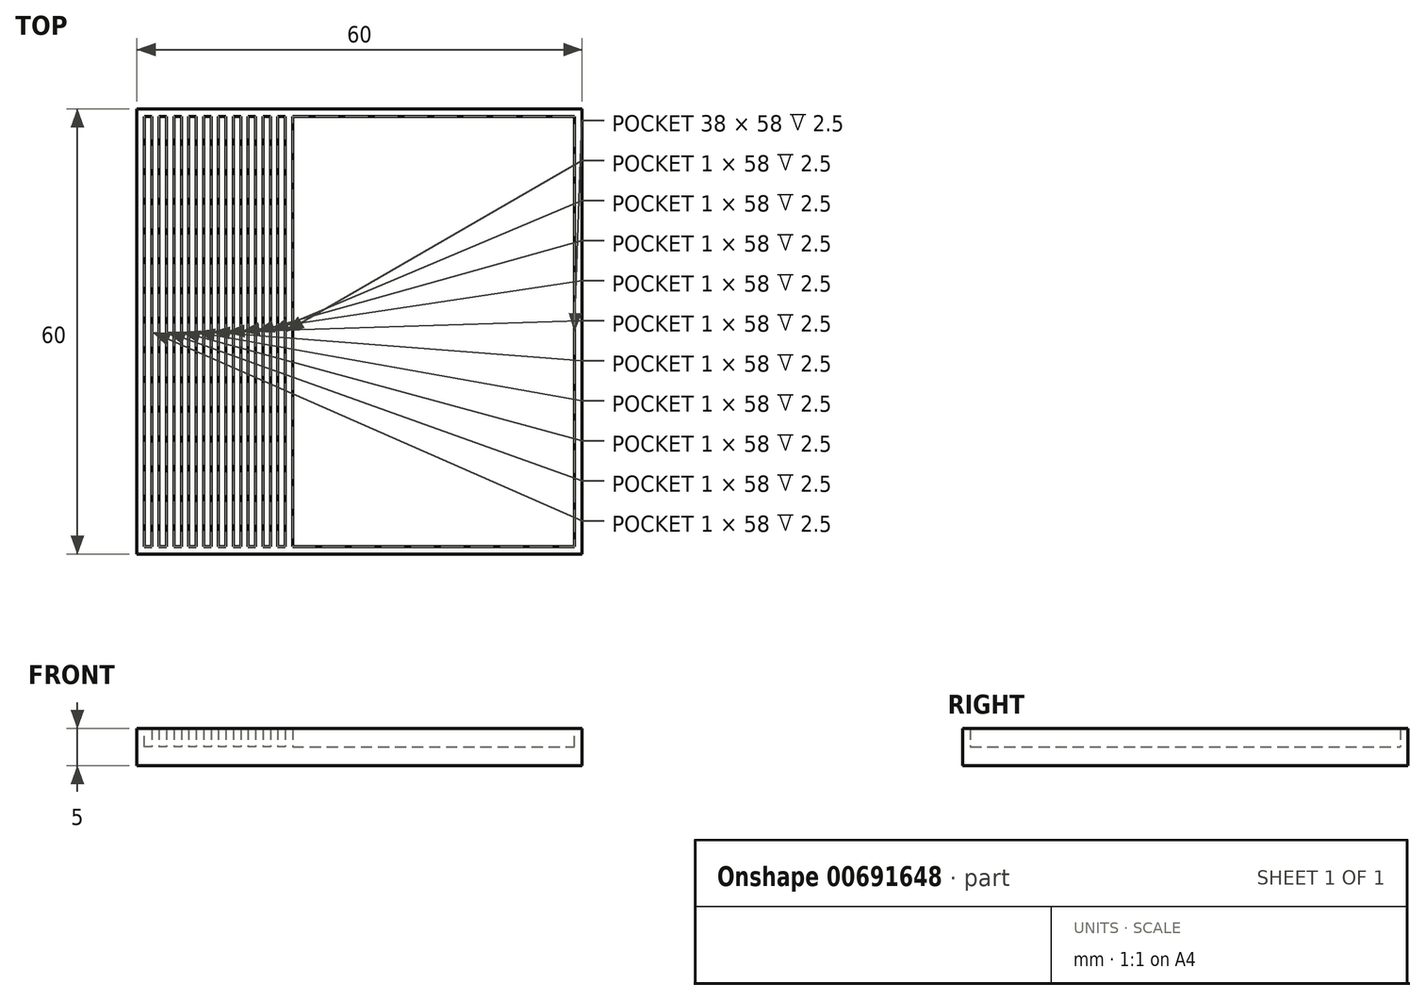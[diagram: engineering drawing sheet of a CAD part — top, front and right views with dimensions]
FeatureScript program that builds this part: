
annotation { "Feature Type Name" : "Feature", "Feature Type Description" : "" }
export const myFeature = defineFeature(function(context is Context, id is Id, definition is map)
    precondition{}
    {
        {
            var Q0;
            Q0=qCreatedBy(makeId("Top.planeOp"),FACE);
            var sketch = newSketch(context, id + "F0", { "sketchPlane" : qUnion([Q0])});
            skLineSegment(sketch, "E0", {"start": v(0, 0) * mm, "end": v(60, 0) * mm});
            skLineSegment(sketch, "E1", {"start": v(60, 0) * mm, "end": v(60, 60) * mm});
            skLineSegment(sketch, "E2", {"start": v(60, 60) * mm, "end": v(0, 60) * mm});
            skLineSegment(sketch, "E3", {"start": v(0, 60) * mm, "end": v(0, 0) * mm});
            skSolve(sketch);
        }
        {
            var Q0;
            Q0=makeQuery(id+"F0.imprint","IMPRINT",FACE,{"disambiguationData":[TD([[makeQuery(id+"F0.imprint","IMPRINT",EDGE,{"derivedFrom":sQuery(id+"F0.wireOp",EDGE,"E0")}),1.0]])]});
            extrude(context, id + "F1", {"entities" : qUnion([Q0]), "depth" : 5 * mm, "offsetDistance" : 25 * mm});
        }
        {
            var Q0;
            Q0=makeQuery(id+"F1.opExtrude","CAP_FACE",FACE,{"disambiguationData":[OSD([sQuery(id+"F0.wireOp",EDGE,"E0"),sQuery(id+"F0.wireOp",EDGE,"E1"),sQuery(id+"F0.wireOp",EDGE,"E2"),sQuery(id+"F0.wireOp",EDGE,"E3")])],"isStart":false});
            var sketch = newSketch(context, id + "F2", { "sketchPlane" : qUnion([Q0])});
            skLineSegment(sketch, "E4", {"start": v(0, 60) * mm, "end": v(1, 60) * mm});
            skLineSegment(sketch, "E5", {"start": v(1, 60) * mm, "end": v(1, 59) * mm});
            skLineSegment(sketch, "E6", {"start": v(1, 59) * mm, "end": v(59, 59) * mm});
            skLineSegment(sketch, "E7", {"start": v(59, 59) * mm, "end": v(59, 1) * mm});
            skLineSegment(sketch, "E8", {"start": v(59, 1) * mm, "end": v(1, 1) * mm});
            skLineSegment(sketch, "E9", {"start": v(1, 1) * mm, "end": v(1, 59) * mm});
            skSolve(sketch);
        }
        {
            var Q0;
            Q0=makeQuery(id+"F2.imprint","IMPRINT",FACE,{"disambiguationData":[TD([[makeQuery(id+"F2.imprint","IMPRINT",EDGE,{"derivedFrom":sQuery(id+"F2.wireOp",EDGE,"E6")}),-1.0]])]});
            extrude(context, id + "F3", {"entities" : qUnion([Q0]), "operationType" : NewBodyOperationType.REMOVE, "oppositeDirection" : true, "depth" : 2.5 * mm, "offsetDistance" : 25 * mm});
        }
        {
            var Q0;
            Q0=makeQuery(id+"F3.boolean.opBoolean","COPY",FACE,{"derivedFrom":makeQuery(id+"F3.opExtrude","CAP_FACE",FACE,{"disambiguationData":[OSD([sQuery(id+"F2.wireOp",EDGE,"E6"),sQuery(id+"F2.wireOp",EDGE,"E7"),sQuery(id+"F2.wireOp",EDGE,"E8"),sQuery(id+"F2.wireOp",EDGE,"E9")])],"isStart":false})});
            var sketch = newSketch(context, id + "F4", { "sketchPlane" : qUnion([Q0])});
            skLineSegment(sketch, "E10", {"start": v(1, 59) * mm, "end": v(2, 59) * mm});
            skLineSegment(sketch, "E11", {"start": v(2, 59) * mm, "end": v(2, 1) * mm});
            skLineSegment(sketch, "E12", {"start": v(2, 1) * mm, "end": v(3, 1) * mm});
            skLineSegment(sketch, "E13", {"start": v(3, 1) * mm, "end": v(3, 59) * mm});
            skLineSegment(sketch, "E14", {"start": v(3, 59) * mm, "end": v(2, 59) * mm});
            skLineSegment(sketch, "E15.1.0.0", {"start": v(4, 59) * mm, "end": v(4, 1) * mm});
            skLineSegment(sketch, "E15.1.0.1", {"start": v(5, 1) * mm, "end": v(5, 59) * mm});
            skLineSegment(sketch, "E15.1.0.2", {"start": v(4, 1) * mm, "end": v(5, 1) * mm});
            skLineSegment(sketch, "E15.1.0.3", {"start": v(5, 59) * mm, "end": v(4, 59) * mm});
            skLineSegment(sketch, "E15.2.0.0", {"start": v(6, 59) * mm, "end": v(6, 1) * mm});
            skLineSegment(sketch, "E15.2.0.1", {"start": v(7, 1) * mm, "end": v(7, 59) * mm});
            skLineSegment(sketch, "E15.2.0.2", {"start": v(6, 1) * mm, "end": v(7, 1) * mm});
            skLineSegment(sketch, "E15.2.0.3", {"start": v(7, 59) * mm, "end": v(6, 59) * mm});
            skLineSegment(sketch, "E15.direction1", {"start": v(2, 1) * mm, "end": v(4, 1) * mm, "construction": true});
            skLineSegment(sketch, "E16.0.3.0", {"start": v(8, 59) * mm, "end": v(8, 1) * mm});
            skLineSegment(sketch, "E16.3.3.0", {"start": v(9, 1) * mm, "end": v(9, 59) * mm});
            skLineSegment(sketch, "E16.6.3.0", {"start": v(8, 1) * mm, "end": v(9, 1) * mm});
            skLineSegment(sketch, "E16.9.3.0", {"start": v(9, 59) * mm, "end": v(8, 59) * mm});
            skLineSegment(sketch, "E16.0.4.0", {"start": v(10, 59) * mm, "end": v(10, 1) * mm});
            skLineSegment(sketch, "E16.3.4.0", {"start": v(11, 1) * mm, "end": v(11, 59) * mm});
            skLineSegment(sketch, "E16.6.4.0", {"start": v(10, 1) * mm, "end": v(11, 1) * mm});
            skLineSegment(sketch, "E16.9.4.0", {"start": v(11, 59) * mm, "end": v(10, 59) * mm});
            skLineSegment(sketch, "E16.0.5.0", {"start": v(12, 59) * mm, "end": v(12, 1) * mm});
            skLineSegment(sketch, "E16.3.5.0", {"start": v(13, 1) * mm, "end": v(13, 59) * mm});
            skLineSegment(sketch, "E16.6.5.0", {"start": v(12, 1) * mm, "end": v(13, 1) * mm});
            skLineSegment(sketch, "E16.9.5.0", {"start": v(13, 59) * mm, "end": v(12, 59) * mm});
            skLineSegment(sketch, "E16.0.6.0", {"start": v(14, 59) * mm, "end": v(14, 1) * mm});
            skLineSegment(sketch, "E16.3.6.0", {"start": v(15, 1) * mm, "end": v(15, 59) * mm});
            skLineSegment(sketch, "E16.6.6.0", {"start": v(14, 1) * mm, "end": v(15, 1) * mm});
            skLineSegment(sketch, "E16.9.6.0", {"start": v(15, 59) * mm, "end": v(14, 59) * mm});
            skLineSegment(sketch, "E16.0.7.0", {"start": v(16, 59) * mm, "end": v(16, 1) * mm});
            skLineSegment(sketch, "E16.3.7.0", {"start": v(17, 1) * mm, "end": v(17, 59) * mm});
            skLineSegment(sketch, "E16.6.7.0", {"start": v(16, 1) * mm, "end": v(17, 1) * mm});
            skLineSegment(sketch, "E16.9.7.0", {"start": v(17, 59) * mm, "end": v(16, 59) * mm});
            skLineSegment(sketch, "E16.0.8.0", {"start": v(18, 59) * mm, "end": v(18, 1) * mm});
            skLineSegment(sketch, "E16.3.8.0", {"start": v(19, 1) * mm, "end": v(19, 59) * mm});
            skLineSegment(sketch, "E16.6.8.0", {"start": v(18, 1) * mm, "end": v(19, 1) * mm});
            skLineSegment(sketch, "E16.9.8.0", {"start": v(19, 59) * mm, "end": v(18, 59) * mm});
            skLineSegment(sketch, "E16.0.9.0", {"start": v(20, 59) * mm, "end": v(20, 1) * mm});
            skLineSegment(sketch, "E16.3.9.0", {"start": v(21, 1) * mm, "end": v(21, 59) * mm});
            skLineSegment(sketch, "E16.6.9.0", {"start": v(20, 1) * mm, "end": v(21, 1) * mm});
            skLineSegment(sketch, "E16.9.9.0", {"start": v(21, 59) * mm, "end": v(20, 59) * mm});
            skSolve(sketch);
        }
        {
            var Q0;
            Q0=makeQuery(id+"F4.imprint","IMPRINT",FACE,{"disambiguationData":[TD([[makeQuery(id+"F4.imprint","IMPRINT",EDGE,{"derivedFrom":sQuery(id+"F4.wireOp",EDGE,"E11")}),1.0]])]});
            var Q1;
            Q1=makeQuery(id+"F4.imprint","IMPRINT",FACE,{"disambiguationData":[TD([[makeQuery(id+"F4.imprint","IMPRINT",EDGE,{"derivedFrom":sQuery(id+"F4.wireOp",EDGE,"E15.1.0.0")}),1.0]])]});
            var Q2;
            Q2=makeQuery(id+"F4.imprint","IMPRINT",FACE,{"disambiguationData":[TD([[makeQuery(id+"F4.imprint","IMPRINT",EDGE,{"derivedFrom":sQuery(id+"F4.wireOp",EDGE,"E15.2.0.0")}),1.0]])]});
            var Q3;
            Q3=makeQuery(id+"F4.imprint","IMPRINT",FACE,{"disambiguationData":[TD([[makeQuery(id+"F4.imprint","IMPRINT",EDGE,{"derivedFrom":sQuery(id+"F4.wireOp",EDGE,"E16.0.3.0")}),1.0]])]});
            var Q4;
            Q4=makeQuery(id+"F4.imprint","IMPRINT",FACE,{"disambiguationData":[TD([[makeQuery(id+"F4.imprint","IMPRINT",EDGE,{"derivedFrom":sQuery(id+"F4.wireOp",EDGE,"E16.0.4.0")}),1.0]])]});
            var Q5;
            Q5=makeQuery(id+"F4.imprint","IMPRINT",FACE,{"disambiguationData":[TD([[makeQuery(id+"F4.imprint","IMPRINT",EDGE,{"derivedFrom":sQuery(id+"F4.wireOp",EDGE,"E16.0.5.0")}),1.0]])]});
            var Q6;
            Q6=makeQuery(id+"F4.imprint","IMPRINT",FACE,{"disambiguationData":[TD([[makeQuery(id+"F4.imprint","IMPRINT",EDGE,{"derivedFrom":sQuery(id+"F4.wireOp",EDGE,"E16.0.6.0")}),1.0]])]});
            var Q7;
            Q7=makeQuery(id+"F4.imprint","IMPRINT",FACE,{"disambiguationData":[TD([[makeQuery(id+"F4.imprint","IMPRINT",EDGE,{"derivedFrom":sQuery(id+"F4.wireOp",EDGE,"E16.0.7.0")}),1.0]])]});
            var Q8;
            Q8=makeQuery(id+"F4.imprint","IMPRINT",FACE,{"disambiguationData":[TD([[makeQuery(id+"F4.imprint","IMPRINT",EDGE,{"derivedFrom":sQuery(id+"F4.wireOp",EDGE,"E16.0.8.0")}),1.0]])]});
            var Q9;
            Q9=makeQuery(id+"F4.imprint","IMPRINT",FACE,{"disambiguationData":[TD([[makeQuery(id+"F4.imprint","IMPRINT",EDGE,{"derivedFrom":sQuery(id+"F4.wireOp",EDGE,"E16.0.9.0")}),1.0]])]});
            extrude(context, id + "F5", {"entities" : qUnion([Q0, Q1, Q2, Q3, Q4, Q5, Q6, Q7, Q8, Q9]), "operationType" : NewBodyOperationType.ADD, "depth" : 2.5 * mm, "offsetDistance" : 25 * mm});
        }
    });
